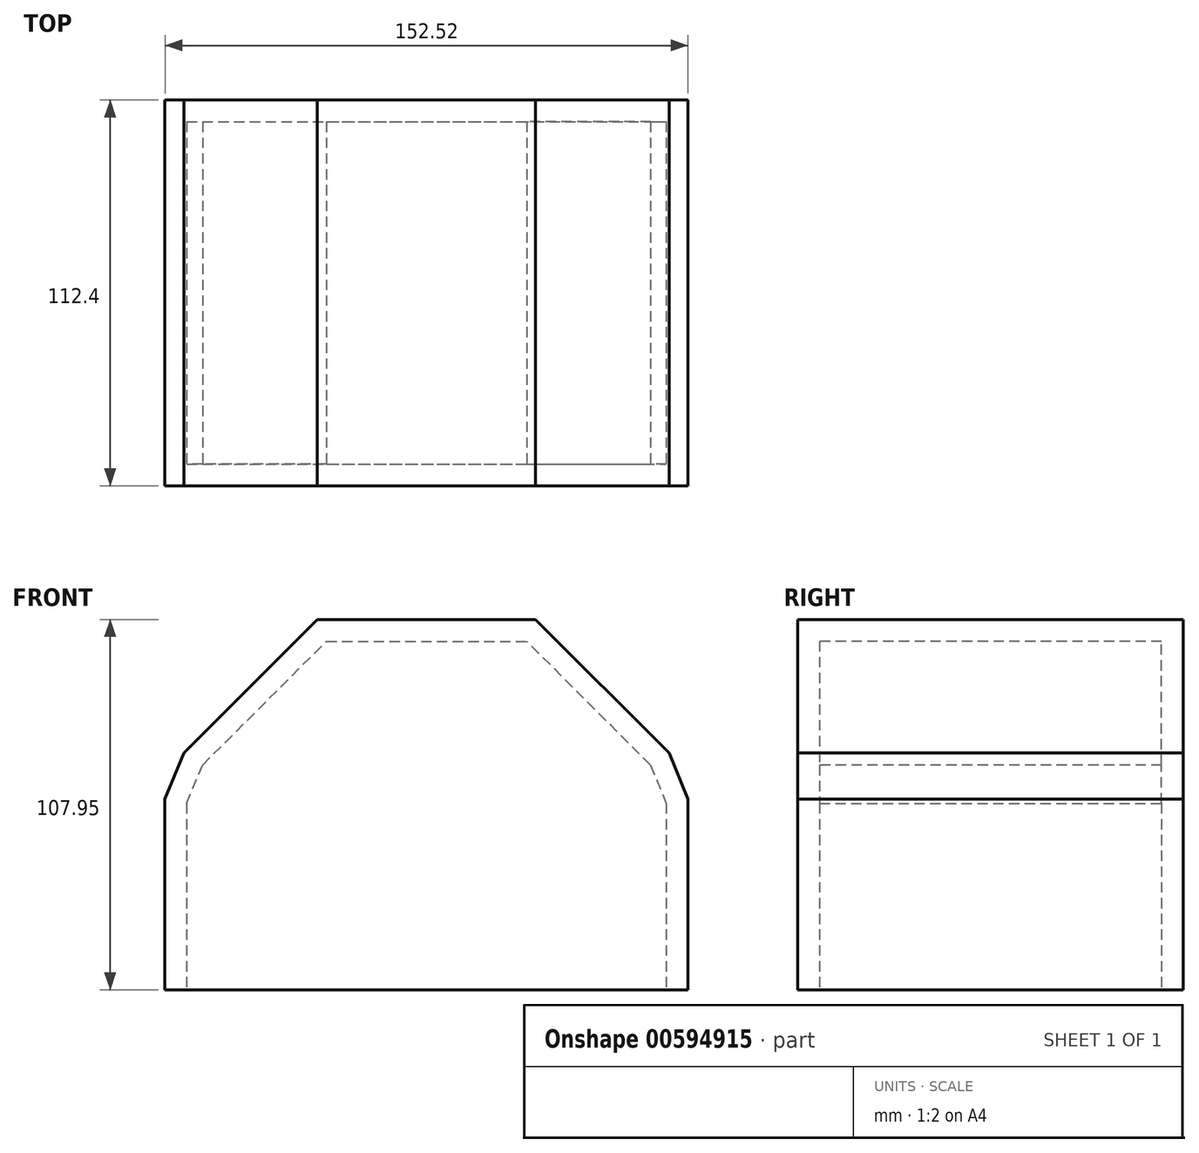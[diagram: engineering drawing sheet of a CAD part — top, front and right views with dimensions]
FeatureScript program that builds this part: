
annotation { "Feature Type Name" : "Feature", "Feature Type Description" : "" }
export const myFeature = defineFeature(function(context is Context, id is Id, definition is map)
    precondition{}
    {
        {
            var Q0;
            Q0=qCreatedBy(makeId("Top.planeOp"),FACE);
            var sketch = newSketch(context, id + "F0", { "sketchPlane" : qUnion([Q0])});
            skLineSegment(sketch, "E0.bottom", {"start": v(-76.26, 56.2) * mm, "end": v(76.26, 56.2) * mm});
            skLineSegment(sketch, "E0.top", {"start": v(-76.26, -56.2) * mm, "end": v(76.26, -56.2) * mm});
            skLineSegment(sketch, "E0.left", {"start": v(-76.26, 56.2) * mm, "end": v(-76.26, -56.2) * mm});
            skLineSegment(sketch, "E0.right", {"start": v(76.26, 56.2) * mm, "end": v(76.26, -56.2) * mm});
            skSolve(sketch);
        }
        {
            var Q0;
            Q0 = qSketchRegion(id + "F0", true);
            extrude(context, id + "F1", {"entities" : qUnion([Q0]), "depth" : 107.95 * mm, "offsetDistance" : 25.4 * mm});
        }
        {
            var Q0;
            Q0=makeQuery(id+"F1.opExtrude","CAP_EDGE",EDGE,{"disambiguationData":[OSD([sQuery(id+"F0.wireOp",EDGE,"E0.left")])],"isStart":false});
            chamfer(context, id + "F2", {"entities" : qUnion([Q0]), "width" : 44.45 * mm, "tangentPropagation" : true});
        }
        {
            var Q0;
            Q0=makeQuery(id+"F1.opExtrude","CAP_EDGE",EDGE,{"disambiguationData":[OSD([sQuery(id+"F0.wireOp",EDGE,"E0.right")])],"isStart":false});
            chamfer(context, id + "F3", {"entities" : qUnion([Q0]), "width" : 44.45 * mm, "tangentPropagation" : true});
        }
        {
            var Q0;
            {var subQ0=sQuery(id+"F0.wireOp",EDGE,"E0.left");Q0=makeQuery(id+"F2.opChamfer","BLEND_EDGE",EDGE,{"blendedFrom":[makeQuery(id+"F1.opExtrude","CAP_EDGE",EDGE,{"disambiguationData":[OSD([subQ0])],"isStart":false}),makeQuery(id+"F1.opExtrude","SWEPT_FACE",FACE,{"disambiguationData":[OSD([subQ0])]})],"blendedInto":[makeQuery(id+"F1.opExtrude","SWEPT_FACE",FACE,{"disambiguationData":[OSD([subQ0])]})]});}
            chamfer(context, id + "F4", {"entities" : qUnion([Q0]), "width" : 19.05 * mm, "tangentPropagation" : true});
        }
        {
            var Q0;
            {var subQ0=sQuery(id+"F0.wireOp",EDGE,"E0.right");Q0=makeQuery(id+"F3.opChamfer","BLEND_EDGE",EDGE,{"blendedFrom":[makeQuery(id+"F1.opExtrude","CAP_EDGE",EDGE,{"disambiguationData":[OSD([subQ0])],"isStart":false}),makeQuery(id+"F1.opExtrude","SWEPT_FACE",FACE,{"disambiguationData":[OSD([subQ0])]})],"blendedInto":[makeQuery(id+"F1.opExtrude","SWEPT_FACE",FACE,{"disambiguationData":[OSD([subQ0])]})]});}
            chamfer(context, id + "F5", {"entities" : qUnion([Q0]), "width" : 19.05 * mm, "tangentPropagation" : true});
        }
        {
            var Q0;
            Q0=makeQuery(id+"F1.opExtrude","CAP_FACE",FACE,{"disambiguationData":[OSD([sQuery(id+"F0.wireOp",EDGE,"E0.bottom"),sQuery(id+"F0.wireOp",EDGE,"E0.top"),sQuery(id+"F0.wireOp",EDGE,"E0.left"),sQuery(id+"F0.wireOp",EDGE,"E0.right")])],"isStart":true});
            shell(context, id + "F6", {"entities" : qUnion([Q0]), "thickness" : 6.35 * mm});
        }
    });
